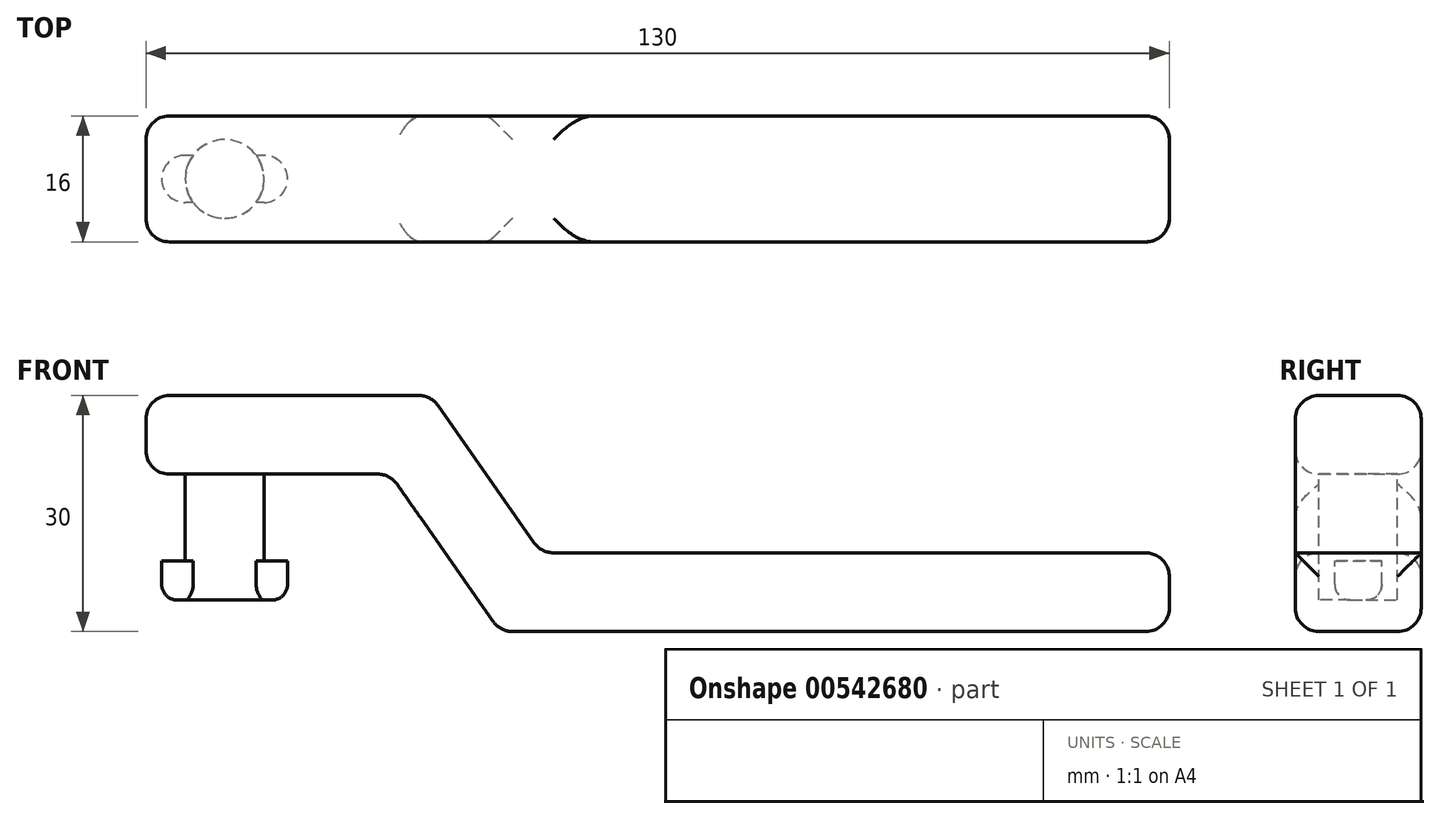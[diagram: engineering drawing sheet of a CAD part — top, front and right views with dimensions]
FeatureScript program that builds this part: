
annotation { "Feature Type Name" : "Feature", "Feature Type Description" : "" }
export const myFeature = defineFeature(function(context is Context, id is Id, definition is map)
    precondition{}
    {
        {
            var Q0;
            Q0=qCreatedBy(makeId("Front.planeOp"),FACE);
            var sketch = newSketch(context, id + "F0", { "sketchPlane" : qUnion([Q0])});
            skLineSegment(sketch, "E0", {"start": v(-10, 0) * mm, "end": v(26.2, 0) * mm});
            skLineSegment(sketch, "E1", {"start": v(26.2, 0) * mm, "end": v(40.2, -20) * mm});
            skLineSegment(sketch, "E2", {"start": v(40.2, -20) * mm, "end": v(120, -20) * mm});
            skLineSegment(sketch, "E3", {"start": v(120, -20) * mm, "end": v(120, -30) * mm});
            skLineSegment(sketch, "E4", {"start": v(120, -30) * mm, "end": v(35, -30) * mm});
            skLineSegment(sketch, "E5", {"start": v(35, -30) * mm, "end": v(21, -10) * mm});
            skLineSegment(sketch, "E6", {"start": v(21, -10) * mm, "end": v(-10, -10) * mm});
            skLineSegment(sketch, "E7", {"start": v(-10, -10) * mm, "end": v(-10, 0) * mm});
            skSolve(sketch);
        }
        {
            var Q0;
            Q0 = qSketchRegion(id + "F0", true);
            extrude(context, id + "F1", {"entities" : qUnion([Q0]), "endBound" : BoundingType.SYMMETRIC, "depth" : 16 * mm, "offsetDistance" : 25 * mm});
        }
        {
            var Q0;
            Q0=makeQuery(id+"F1.opExtrude","SWEPT_FACE",FACE,{"disambiguationData":[OSD([sQuery(id+"F0.wireOp",EDGE,"E6")])]});
            var sketch = newSketch(context, id + "F2", { "sketchPlane" : qUnion([Q0])});
            skCircle(sketch, "E8", {"center": v(0, 0) * mm, "radius": 5 * mm});
            skSolve(sketch);
        }
        {
            var Q0;
            Q0 = qSketchRegion(id + "F2", true);
            extrude(context, id + "F3", {"entities" : qUnion([Q0]), "operationType" : NewBodyOperationType.ADD, "depth" : 11 * mm, "offsetDistance" : 25 * mm});
        }
        {
            var Q0;
            Q0=makeQuery(id+"F3.opExtrude","CAP_FACE",FACE,{"disambiguationData":[OSD([sQuery(id+"F2.wireOp",EDGE,"E8")])],"isStart":false});
            var sketch = newSketch(context, id + "F4", { "sketchPlane" : qUnion([Q0])});
            skCircle(sketch, "E9", {"center": v(0, 0) * mm, "radius": 5 * mm});
            skLineSegment(sketch, "E10.bottom", {"start": v(5, -3) * mm, "end": v(-5, -3) * mm});
            skLineSegment(sketch, "E10.top", {"start": v(5, 3) * mm, "end": v(-5, 3) * mm});
            skLineSegment(sketch, "E10.left", {"start": v(8, 0) * mm, "end": v(8, 0) * mm});
            skLineSegment(sketch, "E10.right", {"start": v(-8, 0) * mm, "end": v(-8, 0) * mm});
            skPoint(sketch, "E11.visualSharp", {"position": v(-8, -3) * mm});
            skArc(sketch, "E11.filletArc", {"start": v(-8, 0) * mm, "mid": v(-7.12, -2.12) * mm, "end": v(-5, -3) * mm});
            skPoint(sketch, "E12.visualSharp", {"position": v(8, 3) * mm});
            skArc(sketch, "E12.filletArc", {"start": v(8, 0) * mm, "mid": v(7.12, 2.12) * mm, "end": v(5, 3) * mm});
            skPoint(sketch, "E13.visualSharp", {"position": v(8, -3) * mm});
            skArc(sketch, "E13.filletArc", {"start": v(5, -3) * mm, "mid": v(7.12, -2.12) * mm, "end": v(8, 0) * mm});
            skPoint(sketch, "E14.visualSharp", {"position": v(-8, 3) * mm});
            skArc(sketch, "E14.filletArc", {"start": v(-5, 3) * mm, "mid": v(-7.12, 2.12) * mm, "end": v(-8, 0) * mm});
            skSolve(sketch);
        }
        {
            var Q0;
            Q0 = qSketchRegion(id + "F4", true);
            extrude(context, id + "F5", {"entities" : qUnion([Q0]), "operationType" : NewBodyOperationType.ADD, "depth" : 5 * mm, "offsetDistance" : 25 * mm});
        }
        {
            var Q0;
            Q0=makeQuery(id+"F1.opExtrude","CAP_EDGE",EDGE,{"disambiguationData":[OSD([sQuery(id+"F0.wireOp",EDGE,"E6")])],"isStart":false});
            var Q1;
            Q1=makeQuery(id+"F1.opExtrude","SWEPT_EDGE",EDGE,{"disambiguationData":[OSD([sQuery(id+"F0.wireOp",EDGE,"E6"),sQuery(id+"F0.wireOp",EDGE,"E7")])]});
            var Q2;
            Q2=makeQuery(id+"F1.opExtrude","CAP_EDGE",EDGE,{"disambiguationData":[OSD([sQuery(id+"F0.wireOp",EDGE,"E6")])],"isStart":true});
            var Q3;
            Q3=makeQuery(id+"F1.opExtrude","SWEPT_EDGE",EDGE,{"disambiguationData":[OSD([sQuery(id+"F0.wireOp",EDGE,"E5"),sQuery(id+"F0.wireOp",EDGE,"E6")])]});
            var Q4;
            Q4=makeQuery(id+"F1.opExtrude","SWEPT_EDGE",EDGE,{"disambiguationData":[OSD([sQuery(id+"F0.wireOp",EDGE,"E4"),sQuery(id+"F0.wireOp",EDGE,"E5")])]});
            var Q5;
            Q5=makeQuery(id+"F1.opExtrude","CAP_EDGE",EDGE,{"disambiguationData":[OSD([sQuery(id+"F0.wireOp",EDGE,"E7")])],"isStart":false});
            var Q6;
            Q6=makeQuery(id+"F1.opExtrude","CAP_EDGE",EDGE,{"disambiguationData":[OSD([sQuery(id+"F0.wireOp",EDGE,"E7")])],"isStart":true});
            var Q7;
            Q7=makeQuery(id+"F1.opExtrude","CAP_EDGE",EDGE,{"disambiguationData":[OSD([sQuery(id+"F0.wireOp",EDGE,"E4")])],"isStart":false});
            var Q8;
            Q8=makeQuery(id+"F1.opExtrude","CAP_EDGE",EDGE,{"disambiguationData":[OSD([sQuery(id+"F0.wireOp",EDGE,"E4")])],"isStart":true});
            var Q9;
            Q9=makeQuery(id+"F1.opExtrude","SWEPT_EDGE",EDGE,{"disambiguationData":[OSD([sQuery(id+"F0.wireOp",EDGE,"E0"),sQuery(id+"F0.wireOp",EDGE,"E7")])]});
            var Q10;
            Q10=makeQuery(id+"F1.opExtrude","CAP_EDGE",EDGE,{"disambiguationData":[OSD([sQuery(id+"F0.wireOp",EDGE,"E0")])],"isStart":false});
            var Q11;
            Q11=makeQuery(id+"F1.opExtrude","CAP_EDGE",EDGE,{"disambiguationData":[OSD([sQuery(id+"F0.wireOp",EDGE,"E0")])],"isStart":true});
            var Q12;
            Q12=makeQuery(id+"F1.opExtrude","SWEPT_EDGE",EDGE,{"disambiguationData":[OSD([sQuery(id+"F0.wireOp",EDGE,"E0"),sQuery(id+"F0.wireOp",EDGE,"E1")])]});
            var Q13;
            Q13=makeQuery(id+"F1.opExtrude","SWEPT_EDGE",EDGE,{"disambiguationData":[OSD([sQuery(id+"F0.wireOp",EDGE,"E1"),sQuery(id+"F0.wireOp",EDGE,"E2")])]});
            var Q14;
            Q14=makeQuery(id+"F1.opExtrude","CAP_EDGE",EDGE,{"disambiguationData":[OSD([sQuery(id+"F0.wireOp",EDGE,"E1")])],"isStart":false});
            var Q15;
            Q15=makeQuery(id+"F1.opExtrude","CAP_EDGE",EDGE,{"disambiguationData":[OSD([sQuery(id+"F0.wireOp",EDGE,"E1")])],"isStart":true});
            var Q16;
            Q16=makeQuery(id+"F1.opExtrude","SWEPT_EDGE",EDGE,{"disambiguationData":[OSD([sQuery(id+"F0.wireOp",EDGE,"E2"),sQuery(id+"F0.wireOp",EDGE,"E3")])]});
            var Q17;
            Q17=makeQuery(id+"F1.opExtrude","CAP_EDGE",EDGE,{"disambiguationData":[OSD([sQuery(id+"F0.wireOp",EDGE,"E3")])],"isStart":false});
            var Q18;
            Q18=makeQuery(id+"F1.opExtrude","SWEPT_EDGE",EDGE,{"disambiguationData":[OSD([sQuery(id+"F0.wireOp",EDGE,"E3"),sQuery(id+"F0.wireOp",EDGE,"E4")])]});
            var Q19;
            Q19=makeQuery(id+"F1.opExtrude","CAP_EDGE",EDGE,{"disambiguationData":[OSD([sQuery(id+"F0.wireOp",EDGE,"E3")])],"isStart":true});
            fillet(context, id + "F6", {"entities" : qUnion([Q0, Q1, Q2, Q3, Q4, Q5, Q6, Q7, Q8, Q9, Q10, Q11, Q12, Q13, Q14, Q15, Q16, Q17, Q18, Q19]), "radius" : 3 * mm, "tangentPropagation" : true, "allowEdgeOverflow" : false});
        }
        {
            var Q0;
            {var subQ0=sQuery(id+"F4.wireOp",EDGE,"E10.top");var subQ1=sQuery(id+"F4.wireOp",EDGE,"E9");Q0=makeQuery(id+"F5.opExtrude","CAP_EDGE",EDGE,{"disambiguationData":[OSD([subQ1]),TDD([makeQuery(id+"F4.imprint","IMPRINT",EDGE,{"disambiguationData":[TD([[makeQuery(id+"F4.imprint","INTERSECT",VERTEX,{"disambiguationData":[OD(0.0)],"derivedFrom":[subQ1,subQ0]}),1.0]])],"derivedFrom":subQ1})])],"isStart":false});}
            var Q1;
            Q1=makeQuery(id+"F5.opExtrude","CAP_EDGE",EDGE,{"disambiguationData":[OSD([sQuery(id+"F4.wireOp",EDGE,"E11.filletArc"),sQuery(id+"F4.wireOp",EDGE,"E14.filletArc")])],"isStart":false});
            var Q2;
            {var subQ0=sQuery(id+"F4.wireOp",EDGE,"E10.bottom");var subQ1=sQuery(id+"F4.wireOp",EDGE,"E9");Q2=makeQuery(id+"F5.opExtrude","CAP_EDGE",EDGE,{"disambiguationData":[OSD([subQ1]),TDD([makeQuery(id+"F4.imprint","IMPRINT",EDGE,{"disambiguationData":[TD([[makeQuery(id+"F4.imprint","INTERSECT",VERTEX,{"disambiguationData":[OD(0.0)],"derivedFrom":[subQ1,subQ0]}),-1.0]])],"derivedFrom":subQ1})])],"isStart":false});}
            var Q3;
            Q3=makeQuery(id+"F5.opExtrude","CAP_EDGE",EDGE,{"disambiguationData":[OSD([sQuery(id+"F4.wireOp",EDGE,"E12.filletArc"),sQuery(id+"F4.wireOp",EDGE,"E13.filletArc")])],"isStart":false});
            fillet(context, id + "F7", {"entities" : qUnion([Q0, Q1, Q2, Q3]), "radius" : 2 * mm, "tangentPropagation" : true, "allowEdgeOverflow" : false});
        }
    });
